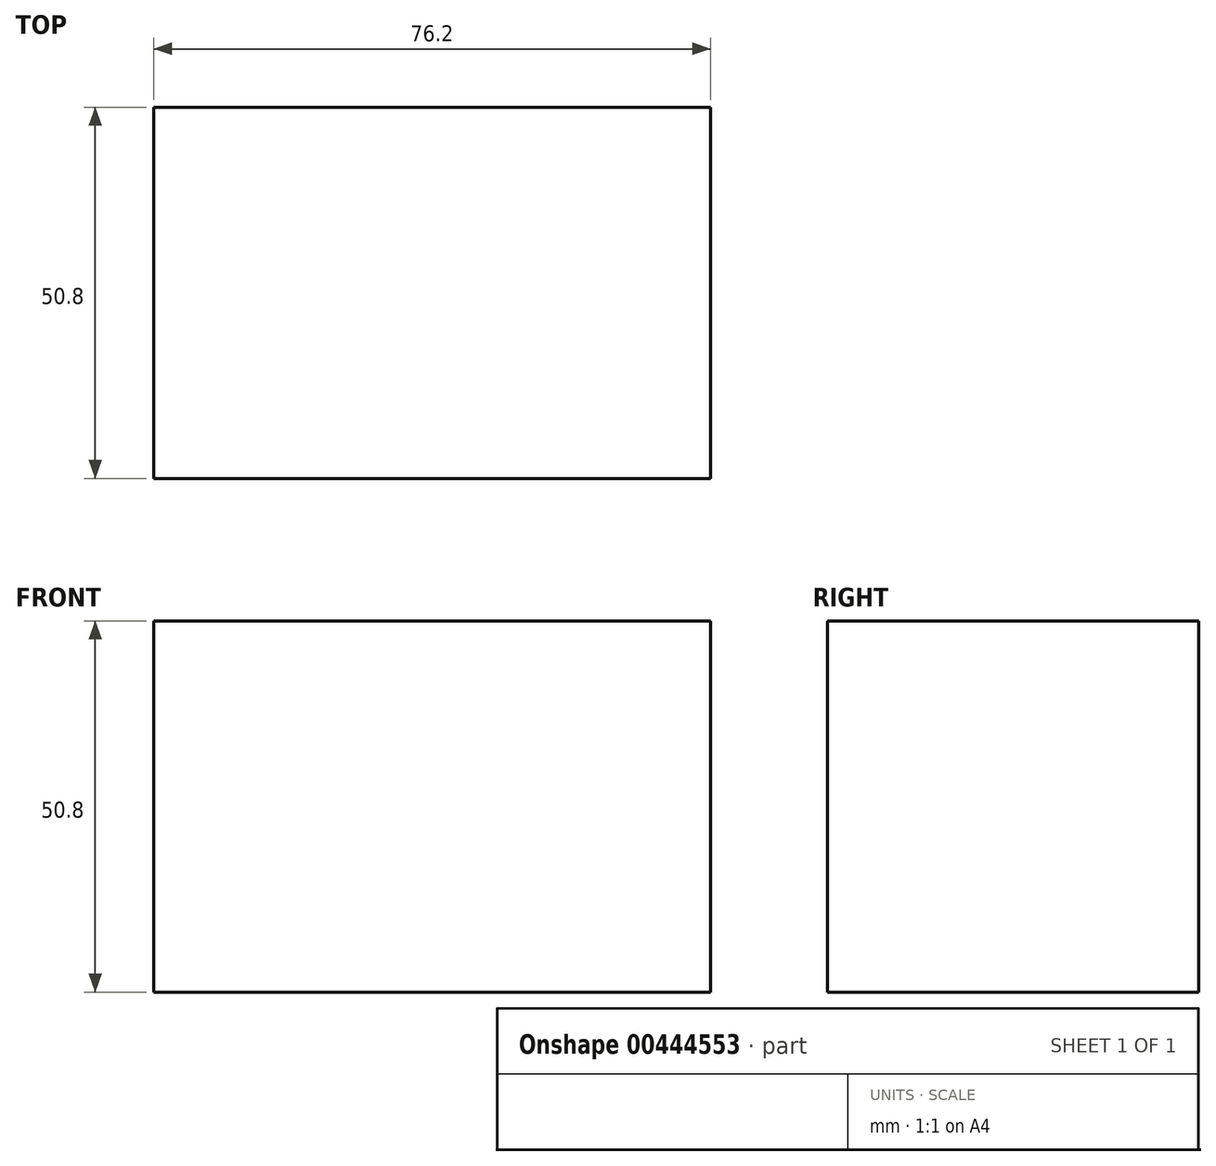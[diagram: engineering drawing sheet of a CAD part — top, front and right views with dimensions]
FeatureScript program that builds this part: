
annotation { "Feature Type Name" : "Feature", "Feature Type Description" : "" }
export const myFeature = defineFeature(function(context is Context, id is Id, definition is map)
    precondition{}
    {
        {
            var Q0;
            Q0=qCreatedBy(makeId("Front.planeOp"),FACE);
            var sketch = newSketch(context, id + "F0", { "sketchPlane" : qUnion([Q0])});
            skLineSegment(sketch, "E0.bottom", {"start": v(0, 0) * mm, "end": v(76.2, 0) * mm});
            skLineSegment(sketch, "E0.top", {"start": v(0, 50.8) * mm, "end": v(76.2, 50.8) * mm});
            skLineSegment(sketch, "E0.left", {"start": v(0, 0) * mm, "end": v(0, 50.8) * mm});
            skLineSegment(sketch, "E0.right", {"start": v(76.2, 0) * mm, "end": v(76.2, 50.8) * mm});
            skSolve(sketch);
        }
        {
            var Q0;
            Q0 = qSketchRegion(id + "F0", true);
            extrude(context, id + "F1", {"entities" : qUnion([Q0]), "depth" : 50.8 * mm});
        }
    });
